# Revit family: SAEX340_76_15
name_source: partatom
category: Detail Items
revit_build: Autodesk Revit 2015 (Build: 20140606_1530(x64)
units: mm (PartAtom-declared; Revit-internal decimal feet)

## types (4) — shared parameters
Density = 0.32 kg
Description = Joist hanger
EPD = https://www.strongtie.eu
ETA / DoP = https://www.strongtie.eu
Manufacturer = Simpson Strong-Tie
Model = SAEX340/76/1.5
Model Disclaimer = Contact Simpson Strong-Tie Company  for more information
Model ID = 0316603553304064569002290455070278947103
Name = SAEX340/76/1.5
ObjectType = SAEX340/76/1.5
Product Material = Stainless steel A4
Product Type = Joist hanger
Reference = SAEX340/76/1,5
Technical datasheet = https://www.strongtie.eu
URL = www.strongtie.eu
UniClass Number = Pr_20_29_31_44
UniClass Title = Joist hangers

## per-type parameters (varying)
| type | _visiblefront | _visibleleft | _visibleright | _visibletop |
| SST_SAEX340/76/1.5_Front | Yes | No | No | No |
| SST_SAEX340/76/1.5_Top | No | No | No | Yes |
| SST_SAEX340/76/1.5_Left | No | Yes | No | No |
| SST_SAEX340/76/1.5_Right | No | No | Yes | No |

## geometry (parser evidence)
native form markers: Sweep x2
no freeform markers — native parametric forms only
